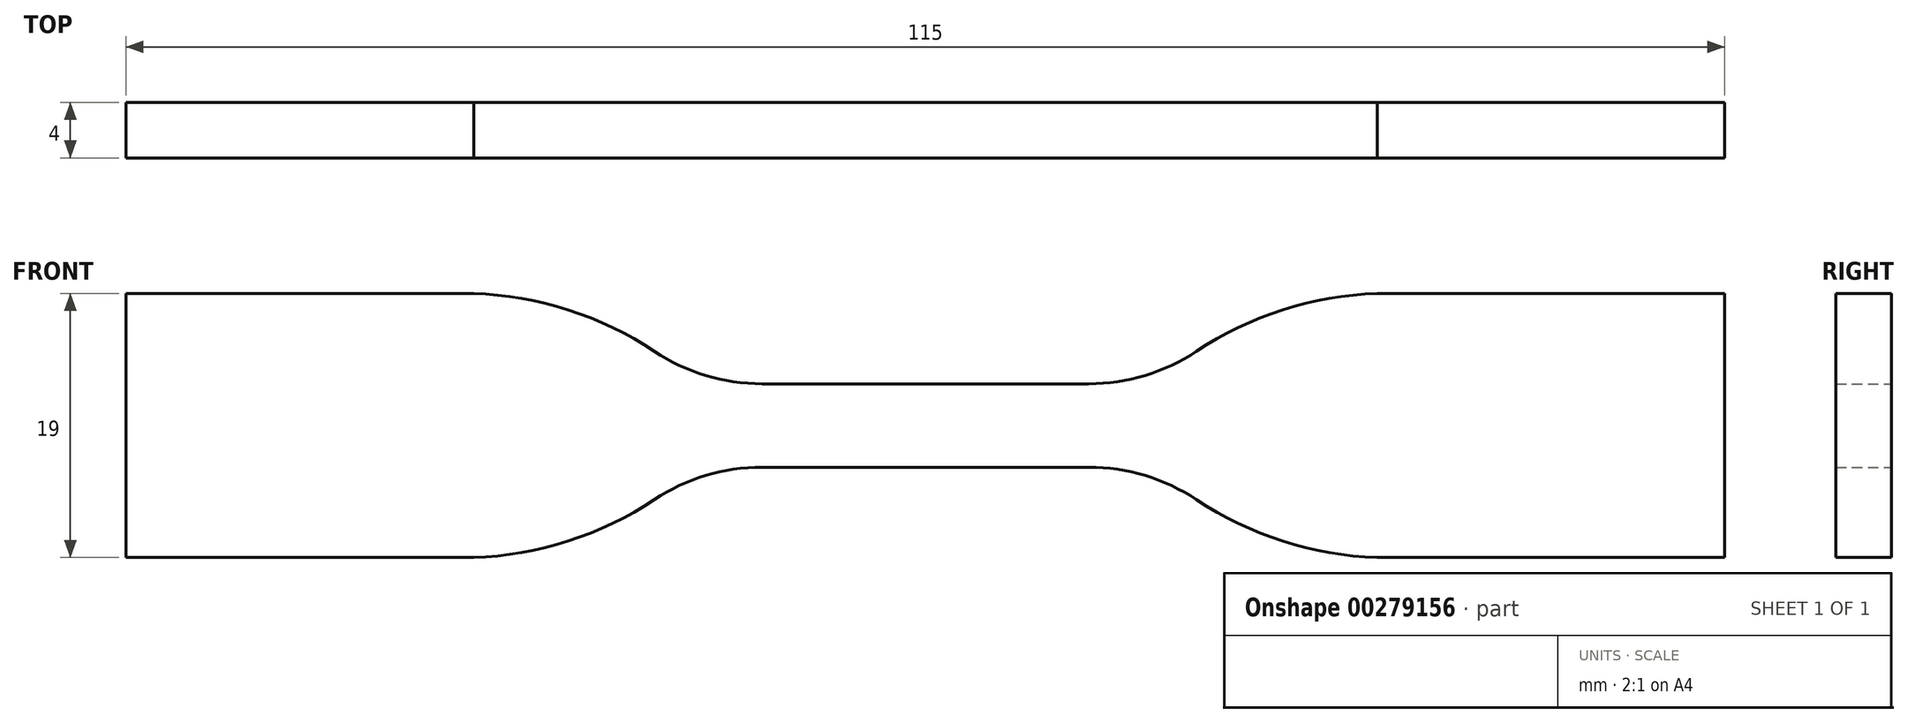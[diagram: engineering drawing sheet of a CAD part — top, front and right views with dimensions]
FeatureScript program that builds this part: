
annotation { "Feature Type Name" : "Feature", "Feature Type Description" : "" }
export const myFeature = defineFeature(function(context is Context, id is Id, definition is map)
    precondition{}
    {
        {
            var Q0;
            Q0=qCreatedBy(makeId("Front.planeOp"),FACE);
            var sketch = newSketch(context, id + "F0", { "sketchPlane" : qUnion([Q0])});
            skLineSegment(sketch, "E0", {"start": v(0, 3) * mm, "end": v(11.75, 3) * mm});
            skArc(sketch, "E1", {"start": v(32.5, 9.5) * mm, "mid": v(25.7, 8.32) * mm, "end": v(19.5, 5.34) * mm});
            skLineSegment(sketch, "E2", {"start": v(32.5, 9.5) * mm, "end": v(57.5, 9.5) * mm});
            skLineSegment(sketch, "E3.MirrorCS", {"start": v(32.5, -9.5) * mm, "end": v(57.5, -9.5) * mm});
            skLineSegment(sketch, "E4.MirrorCS", {"start": v(0, -3) * mm, "end": v(11.75, -3) * mm});
            skArc(sketch, "E5.MirrorCS", {"start": v(32.5, -9.5) * mm, "mid": v(25.7, -8.32) * mm, "end": v(19.5, -5.34) * mm});
            skArc(sketch, "E6.MirrorCS", {"start": v(-32.5, -9.5) * mm, "mid": v(-25.7, -8.32) * mm, "end": v(-19.5, -5.34) * mm});
            skLineSegment(sketch, "E7.MirrorCS", {"start": v(0, 3) * mm, "end": v(-11.75, 3) * mm});
            skArc(sketch, "E8.MirrorCS", {"start": v(-32.5, 9.5) * mm, "mid": v(-25.7, 8.32) * mm, "end": v(-19.5, 5.34) * mm});
            skLineSegment(sketch, "E9.MirrorCS", {"start": v(-32.5, -9.5) * mm, "end": v(-57.5, -9.5) * mm});
            skLineSegment(sketch, "E10.MirrorCS", {"start": v(0, -3) * mm, "end": v(-11.75, -3) * mm});
            skLineSegment(sketch, "E11.MirrorCS", {"start": v(-32.5, 9.5) * mm, "end": v(-57.5, 9.5) * mm});
            skLineSegment(sketch, "E12", {"start": v(-57.5, 9.5) * mm, "end": v(-57.5, -9.5) * mm});
            skLineSegment(sketch, "E13", {"start": v(57.5, 9.5) * mm, "end": v(57.5, -9.5) * mm});
            skPoint(sketch, "E14.visualSharp", {"position": v(-16.5, 3) * mm});
            skArc(sketch, "E14.filletArc", {"start": v(-19.5, 5.34) * mm, "mid": v(-15.8, 3.6) * mm, "end": v(-11.75, 3) * mm});
            skPoint(sketch, "E15.visualSharp", {"position": v(16.5, 3) * mm});
            skArc(sketch, "E15.filletArc", {"start": v(11.75, 3) * mm, "mid": v(15.8, 3.6) * mm, "end": v(19.5, 5.34) * mm});
            skPoint(sketch, "E16.visualSharp", {"position": v(16.5, -3) * mm});
            skArc(sketch, "E16.filletArc", {"start": v(19.5, -5.34) * mm, "mid": v(15.8, -3.6) * mm, "end": v(11.75, -3) * mm});
            skPoint(sketch, "E17.visualSharp", {"position": v(-16.5, -3) * mm});
            skArc(sketch, "E17.filletArc", {"start": v(-11.75, -3) * mm, "mid": v(-15.8, -3.6) * mm, "end": v(-19.5, -5.34) * mm});
            skSolve(sketch);
        }
        {
            var Q0;
            Q0=makeQuery(id+"F0.imprint","IMPRINT",FACE,{"disambiguationData":[TD([[makeQuery(id+"F0.imprint","IMPRINT",EDGE,{"derivedFrom":sQuery(id+"F0.wireOp",EDGE,"E0")}),-1.0]])]});
            extrude(context, id + "F1", {"entities" : qUnion([Q0]), "endBound" : BoundingType.SYMMETRIC, "depth" : 4 * mm});
        }
    });
